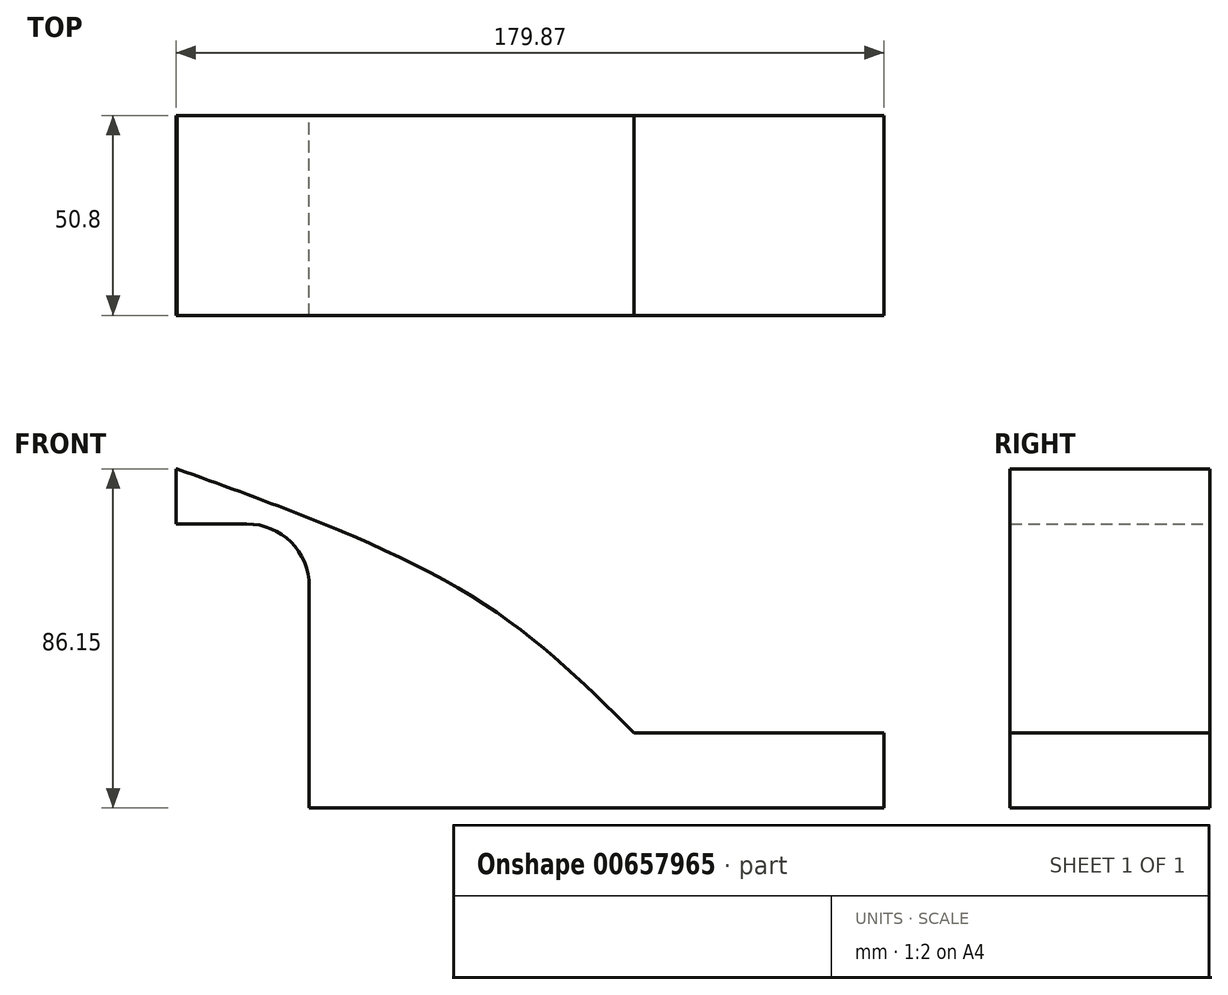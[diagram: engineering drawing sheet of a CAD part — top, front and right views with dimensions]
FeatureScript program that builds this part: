
annotation { "Feature Type Name" : "Feature", "Feature Type Description" : "" }
export const myFeature = defineFeature(function(context is Context, id is Id, definition is map)
    precondition{}
    {
        {
            var Q0;
            Q0=qCreatedBy(makeId("Front.planeOp"),FACE);
            var sketch = newSketch(context, id + "F0", { "sketchPlane" : qUnion([Q0])});
            skLineSegment(sketch, "E0.bottom", {"start": v(-41.28, -9.52) * mm, "end": v(41.28, -9.52) * mm});
            skLineSegment(sketch, "E0.top", {"start": v(-41.28, 9.52) * mm, "end": v(41.28, 9.52) * mm});
            skLineSegment(sketch, "E0.left", {"start": v(-41.28, -9.52) * mm, "end": v(-41.28, 9.52) * mm});
            skLineSegment(sketch, "E0.right", {"start": v(41.28, -9.52) * mm, "end": v(41.28, 9.52) * mm});
            skPoint(sketch, "E0.middle", {"position": v(0, 0) * mm});
            skPoint(sketch, "E1.middle", {"position": v(-41.28, -9.52) * mm});
            skLineSegment(sketch, "E2.bottom", {"start": v(-75.1, 76.93) * mm, "end": v(-125.9, 76.93) * mm});
            skLineSegment(sketch, "E2.top", {"start": v(-75.1, 48.36) * mm, "end": v(-125.9, 48.36) * mm});
            skLineSegment(sketch, "E2.left", {"start": v(-75.1, 76.93) * mm, "end": v(-75.1, 48.36) * mm});
            skLineSegment(sketch, "E2.right", {"start": v(-125.9, 76.93) * mm, "end": v(-125.9, 48.36) * mm});
            skLineSegment(sketch, "E3", {"start": v(-41.28, 0) * mm, "end": v(-41.28, 46.77) * mm});
            skLineSegment(sketch, "E4", {"start": v(-57.15, 62.65) * mm, "end": v(-93.43, 62.65) * mm});
            skArc(sketch, "E5", {"start": v(-41.28, 46.77) * mm, "mid": v(-45.92, 58) * mm, "end": v(-57.15, 62.65) * mm});
            skLineSegment(sketch, "E6.bottom", {"start": v(-125.9, 48.36) * mm, "end": v(-75.67, 48.36) * mm});
            skLineSegment(sketch, "E6.top", {"start": v(-125.9, 76.93) * mm, "end": v(-75.67, 76.93) * mm});
            skLineSegment(sketch, "E6.left", {"start": v(-125.9, 48.36) * mm, "end": v(-125.9, 76.93) * mm});
            skLineSegment(sketch, "E6.right", {"start": v(-75.67, 48.36) * mm, "end": v(-75.67, 76.93) * mm});
            skPoint(sketch, "E6.middle", {"position": v(-100.78, 62.65) * mm});
            skPoint(sketch, "E6.middle.positionSnap0", {"position": v(-75.1, 62.65) * mm});
            skPoint(sketch, "E6.centerSnap0", {"position": v(-75.1, 62.65) * mm});
            skLineSegment(sketch, "E7.0", {"start": v(-57.15, 76.62) * mm, "end": v(-93.43, 76.62) * mm});
            skArc(sketch, "E7.1", {"start": v(-27.3, 46.77) * mm, "mid": v(-36.05, 67.88) * mm, "end": v(-57.15, 76.62) * mm});
            skLineSegment(sketch, "E7.2", {"start": v(-27.3, 0) * mm, "end": v(-27.3, 46.77) * mm});
            skLineSegment(sketch, "E8", {"start": v(-93.43, 62.65) * mm, "end": v(-93.43, 76.62) * mm});
            skFitSpline(sketch, "E9", {"points": [v(41.28, 9.52) * mm, v(0, 44.3) * mm, v(-75.67, 76.93) * mm], "startDerivative": vector(-82.3, 81.92) * mm, "endDerivative": vector(-149.24, 53.88) * mm});
            skSolve(sketch);
        }
        {
            var Q0;
            Q0=makeQuery(id+"F0.imprint","IMPRINT",FACE,{"disambiguationData":[TD([[makeQuery(id+"F0.imprint","IMPRINT",EDGE,{"derivedFrom":sQuery(id+"F0.wireOp",EDGE,"E0.bottom")}),1.0]])]});
            var Q1;
            {var subQ0=sQuery(id+"F0.wireOp",EDGE,"E5");Q1=makeQuery(id+"F0.imprint","IMPRINT",FACE,{"disambiguationData":[TD([[makeQuery(id+"F0.imprint","IMPRINT",EDGE,{"derivedFrom":subQ0}),-1.0]])]});}
            var Q2;
            {var subQ3=sQuery(id+"F0.wireOp",EDGE,"E7.2");var subQ5=sQuery(id+"F0.wireOp",EDGE,"E7.1");var subQ6=makeQuery(id+"F0.imprint","INTERSECT",VERTEX,{"derivedFrom":[subQ3,subQ5]});Q2=makeQuery(id+"F0.imprint","IMPRINT",FACE,{"disambiguationData":[TD([[makeQuery(id+"F0.imprint","IMPRINT",EDGE,{"disambiguationData":[TD([[subQ6,1.0]])],"derivedFrom":subQ3}),-1.0]])]});}
            extrude(context, id + "F1", {"entities" : qUnion([Q0, Q1, Q2]), "endBound" : BoundingType.SYMMETRIC, "depth" : 50.8 * mm, "offsetDistance" : 25.4 * mm, "hasSecondDirection" : true, "secondDirectionOppositeDirection" : true, "secondDirectionDepth" : 25.4 * mm});
        }
        {
            var Q0;
            Q0=makeQuery(id+"F1.opExtrude","SWEPT_FACE",FACE,{"disambiguationData":[OSD([sQuery(id+"F0.wireOp",EDGE,"E0.right")])]});
            extrude(context, id + "F2", {"entities" : qUnion([Q0]), "operationType" : NewBodyOperationType.ADD, "endBound" : BoundingType.SYMMETRIC, "depth" : 127 * mm, "offsetDistance" : 25.4 * mm});
        }
    });
